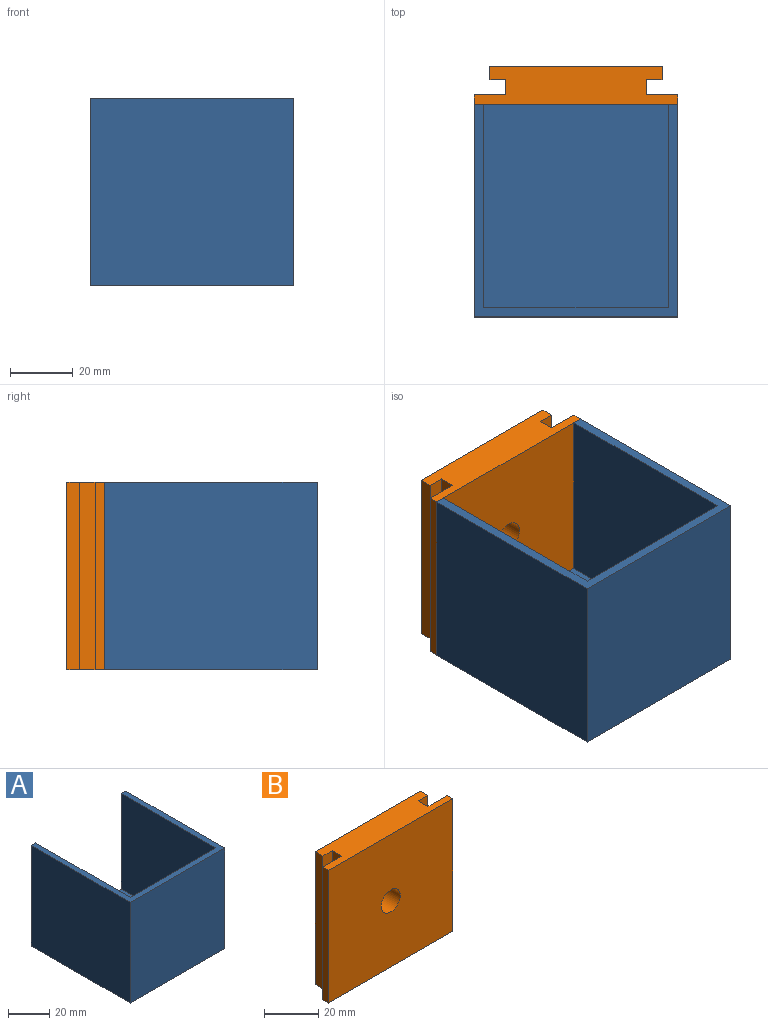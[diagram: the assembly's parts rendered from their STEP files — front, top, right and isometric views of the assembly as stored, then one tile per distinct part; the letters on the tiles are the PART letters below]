
ASSEMBLY  parts=2 mates=1
PART A: 10 faces, bbox 65x68x60 mm
  f0: plane 68x65mm, normal (0,0,-1), area 4420mm2, adj f1,f3,f4,f9
  f1: plane 68x60mm, normal (1,0,0), area 4080mm2, adj f0,f2,f4,f9
  f2: plane 68x65mm, normal (0,0,1), area 585mm2, adj f1,f3,f4,f5,f6,f7,f9
  f3: plane 68x60mm, normal (-1,0,0), area 4080mm2, adj f0,f2,f4,f9
  f4: plane 65x60mm, normal (0,-1,0), area 3900mm2, adj f0,f1,f2,f3
  f5: plane 59x57mm, normal (0,1,0), area 3363mm2, adj f2,f6,f7,f8
  f6: plane 65x57mm, normal (-1,0,0), area 3705mm2, adj f2,f5,f8,f9
  f7: plane 65x57mm, normal (1,0,0), area 3705mm2, adj f2,f5,f8,f9
  f8: plane 65x59mm, normal (0,0,1), area 3835mm2, adj f5,f6,f7,f9
  f9: plane 65x60mm, normal (0,1,0), area 537mm2, adj f0,f1,f2,f3,f6,f7,f8
PART B: 15 faces, bbox 65x12x60 mm
  f0: plane 60x10mm, normal (0,1,0), area 600mm2, adj f1,f3,f5,f8
  f1: plane 65x12mm, normal (0,0,-1), area 640mm2, adj f0,f2,f5,f6,f7,f8,f9,f10
  f2: plane 60x3mm, normal (1,0,0), area 180mm2, adj f1,f3,f6,f7
  f3: plane 65x12mm, normal (0,0,1), area 640mm2, adj f0,f2,f5,f6,f7,f8,f9,f10
  f4: cylinder r=5mm len=12mm, axis (0,1,0), area 377mm2, adj f6,f13
  f5: plane 60x3mm, normal (-1,0,0), area 180mm2, adj f0,f1,f3,f6
  f6: plane 65x60mm, normal (0,-1,0), area 3821.5mm2, adj f1,f2,f3,f4,f5
  f7: plane 60x10mm, normal (0,1,0), area 600mm2, adj f1,f2,f3,f9
  f8: plane 60x5mm, normal (-1,0,0), area 300mm2, adj f0,f1,f3,f10
  f9: plane 60x5mm, normal (1,0,0), area 300mm2, adj f1,f3,f7,f14
  f10: plane 60x5mm, normal (0,-1,0), area 300mm2, adj f1,f3,f8,f11
  f11: plane 60x4mm, normal (-1,0,0), area 240mm2, adj f1,f3,f10,f13
  f12: plane 60x4mm, normal (1,0,0), area 240mm2, adj f1,f3,f13,f14
  f13: plane 60x55mm, normal (0,1,0), area 3221.5mm2, adj f1,f3,f4,f11,f12
  f14: plane 60x5mm, normal (0,-1,0), area 300mm2, adj f1,f3,f9,f12
PLACE A t=(-5.51,-70.08,6.15)mm
PLACE B t=(-5.51,-2.08,6.15)mm fixed
MATE fastened A.f9 <-> B.f6  axis (0,1,0) through (-38.01,-5.08,36.15)mm
